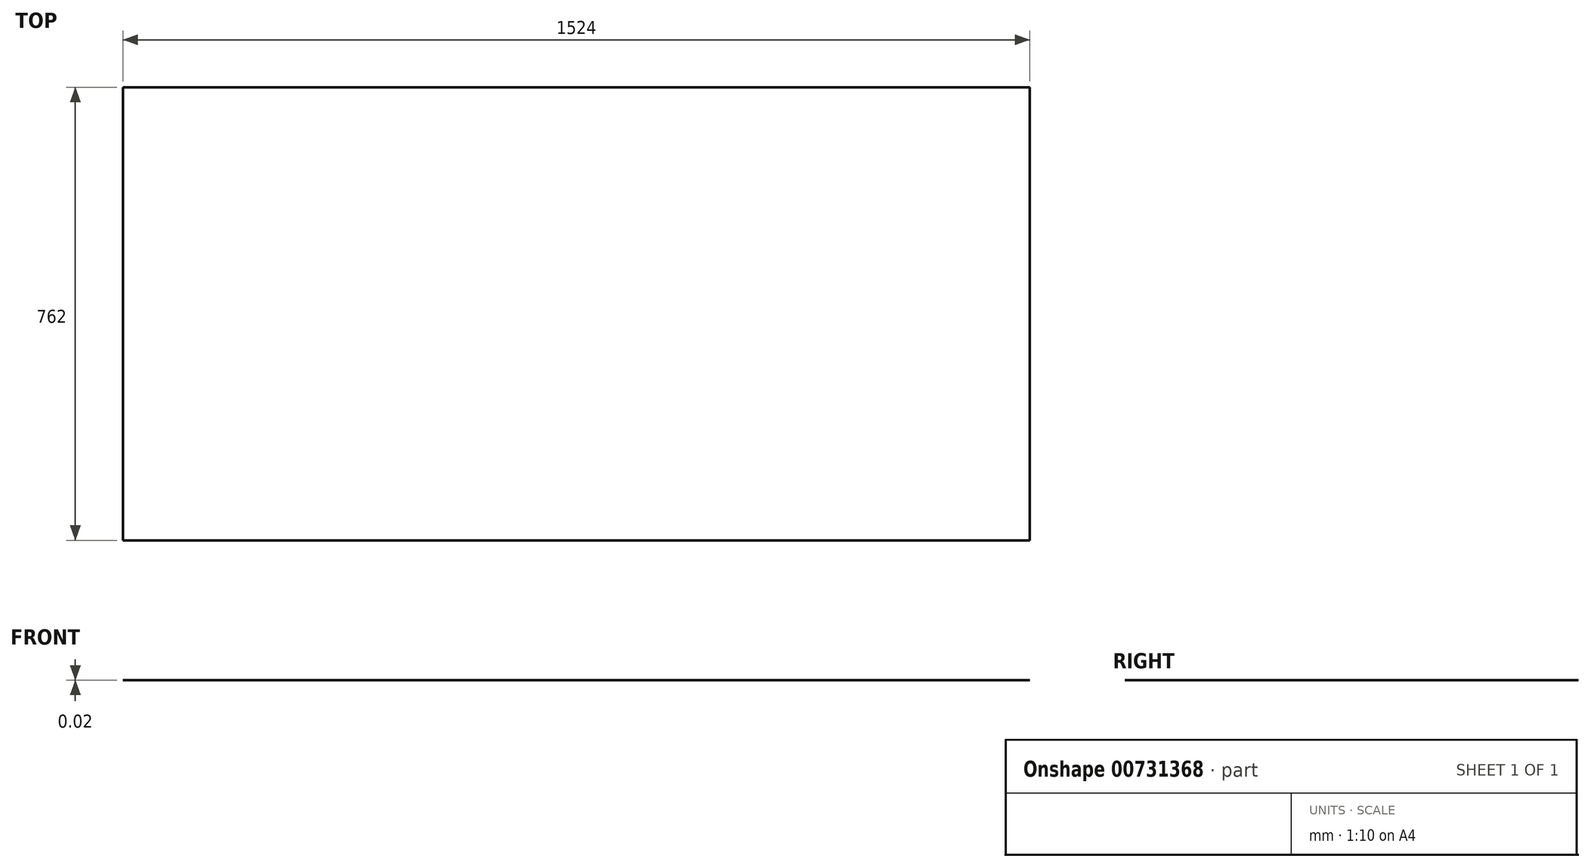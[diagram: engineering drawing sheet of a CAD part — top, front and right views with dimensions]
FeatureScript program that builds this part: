
annotation { "Feature Type Name" : "Feature", "Feature Type Description" : "" }
export const myFeature = defineFeature(function(context is Context, id is Id, definition is map)
    precondition{}
    {
        {
            var Q0;
            Q0=qCreatedBy(makeId("Top.planeOp"),FACE);
            var sketch = newSketch(context, id + "F0", { "sketchPlane" : qUnion([Q0])});
            skLineSegment(sketch, "E0.bottom", {"start": v(-762, 381) * mm, "end": v(762, 381) * mm});
            skLineSegment(sketch, "E0.top", {"start": v(-762, -381) * mm, "end": v(762, -381) * mm});
            skLineSegment(sketch, "E0.left", {"start": v(-762, 381) * mm, "end": v(-762, -381) * mm});
            skLineSegment(sketch, "E0.right", {"start": v(762, 381) * mm, "end": v(762, -381) * mm});
            skPoint(sketch, "E0.middle", {"position": v(0, 0) * mm});
            skSolve(sketch);
        }
        {
            var Q0;
            Q0 = qSketchRegion(id + "F0", true);
            extrude(context, id + "F1", {"entities" : qUnion([Q0]), "depth" : 1 / 50.8 * mm, "offsetDistance" : 25.4 * mm});
        }
    });
